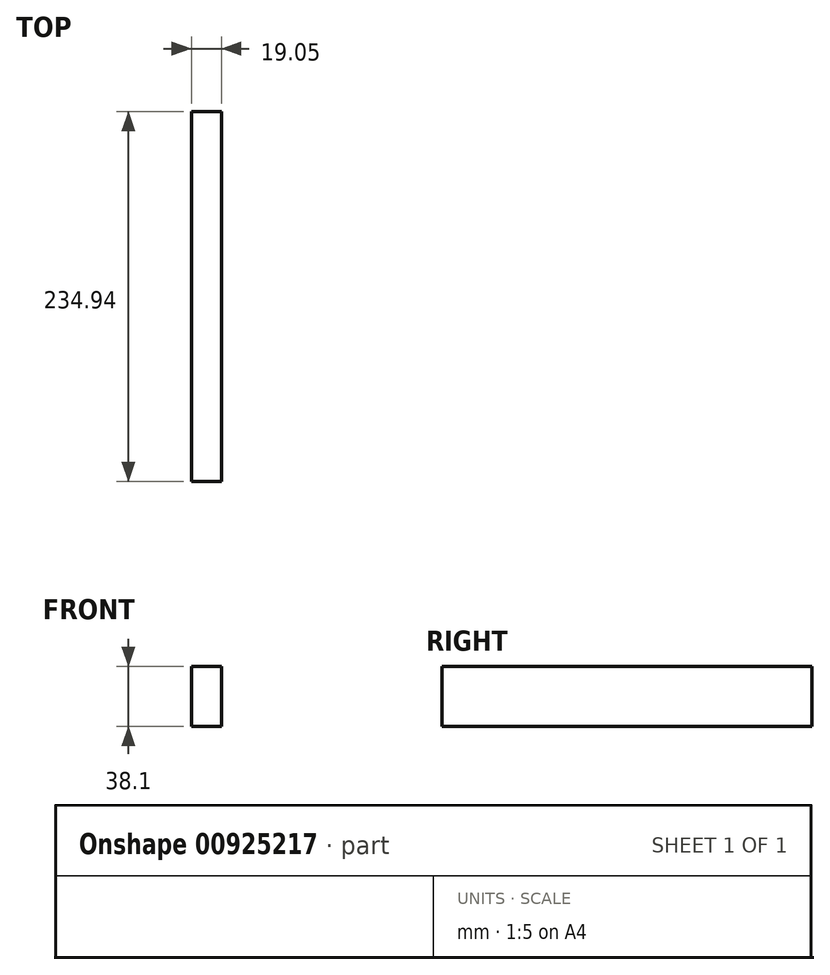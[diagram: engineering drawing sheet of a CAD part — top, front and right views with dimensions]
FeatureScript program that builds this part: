
annotation { "Feature Type Name" : "Feature", "Feature Type Description" : "" }
export const myFeature = defineFeature(function(context is Context, id is Id, definition is map)
    precondition{}
    {
        {
            var Q0;
            Q0=qCreatedBy(makeId("Right.planeOp"),FACE);
            var sketch = newSketch(context, id + "F0", { "sketchPlane" : qUnion([Q0])});
            skLineSegment(sketch, "E0.bottom", {"start": v(117.48, -19.05) * mm, "end": v(-117.47, -19.05) * mm});
            skLineSegment(sketch, "E0.top", {"start": v(117.47, 19.05) * mm, "end": v(-117.47, 19.05) * mm});
            skLineSegment(sketch, "E0.left", {"start": v(117.48, -19.05) * mm, "end": v(117.48, 19.05) * mm});
            skLineSegment(sketch, "E0.right", {"start": v(-117.47, -19.05) * mm, "end": v(-117.47, 19.05) * mm});
            skPoint(sketch, "E0.middle", {"position": v(0, 0) * mm});
            skSolve(sketch);
        }
        {
            var Q0;
            Q0 = qSketchRegion(id + "F0", true);
            extrude(context, id + "F1", {"entities" : qUnion([Q0]), "depth" : 19.05 * mm, "offsetDistance" : 25.4 * mm});
        }
    });
